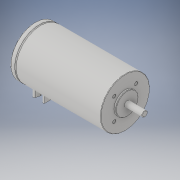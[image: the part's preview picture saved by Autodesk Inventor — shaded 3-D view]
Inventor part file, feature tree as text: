
AUTODESK INVENTOR PART (.ipt)
format: ipt  version: 2018 (Build 220112000, 112)  size: 181,248 bytes
history: native  units: in
note: dims shown in document units (in); Inventor stores cm internally (conversion verified against a paired STEP export)
features: extrude x1, sketch x1, imported_body x1
ambient origin geometry x8: Origin, YZ Plane, XZ Plane, XY Plane, X Axis, Y Axis, Z Axis, Center Point
bodies: Solid1 (feature_tree)
feature tree (3):
  extrude  "Extrusion1"  [1 undecoded]
  sketch  "Sketch1"  dims[d0=0.3937in d1=0.0in]
  imported_body  "Base1"
note: 1 required parameter value undecoded (feature->parameter linkage not recoverable at this tier; creation-order binding heuristic only, values carry confidence <= 0.55)
